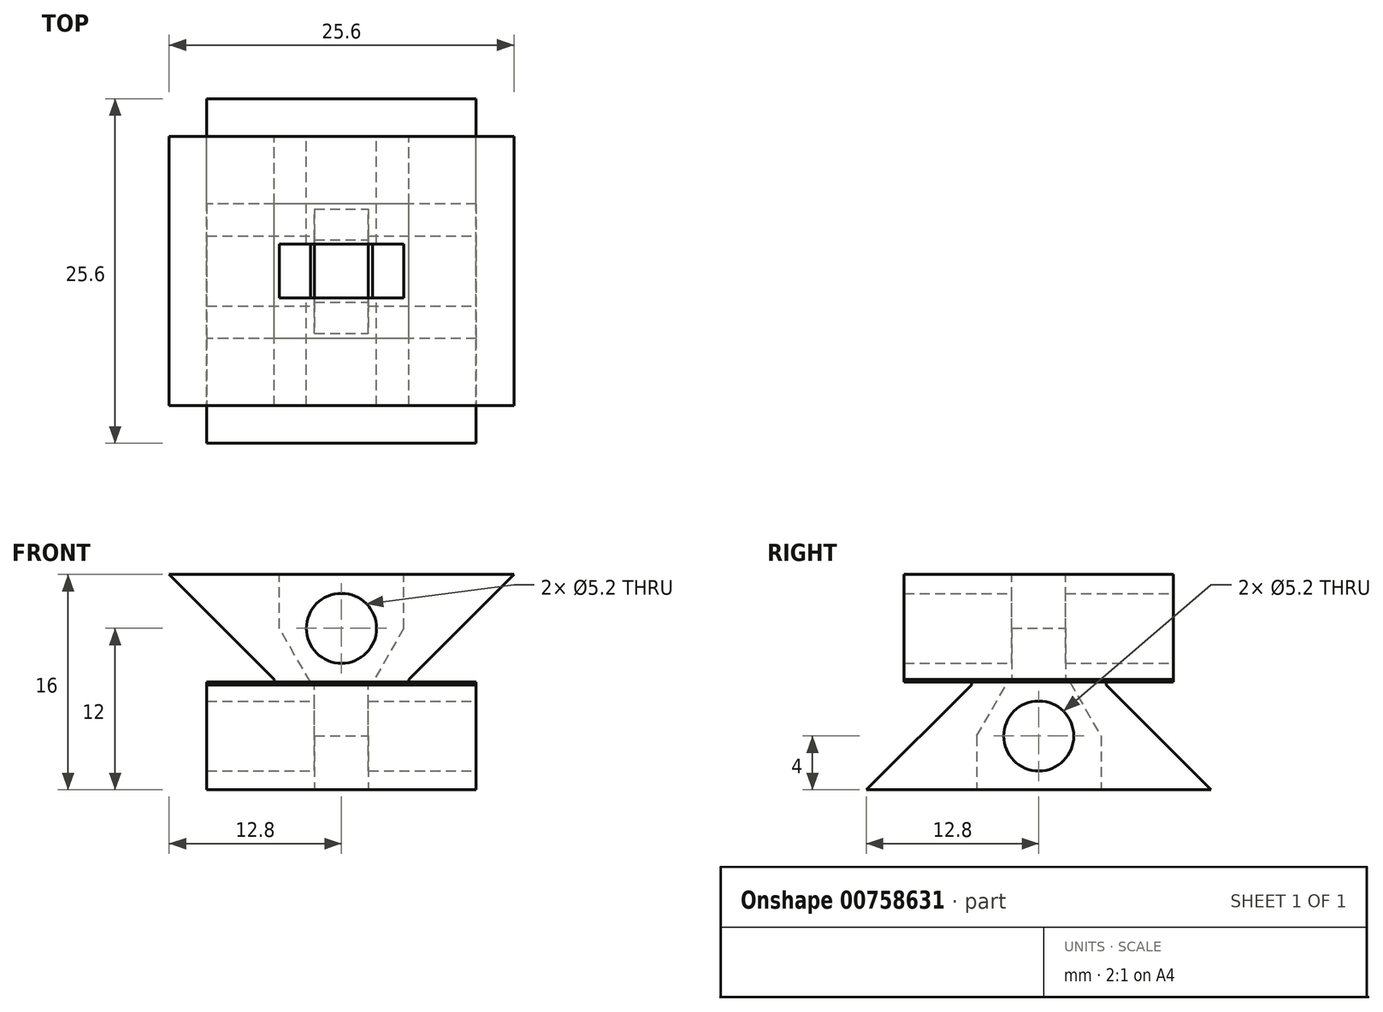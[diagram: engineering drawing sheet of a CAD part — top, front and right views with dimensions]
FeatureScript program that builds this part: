
annotation { "Feature Type Name" : "Feature", "Feature Type Description" : "" }
export const myFeature = defineFeature(function(context is Context, id is Id, definition is map)
    precondition{}
    {
        {
            var Q0;
            Q0=qCreatedBy(makeId("Front.planeOp"),FACE);
            var sketch = newSketch(context, id + "F0", { "sketchPlane" : qUnion([Q0])});
            skLineSegment(sketch, "E0", {"start": v(0, 8) * mm, "end": v(12.8, 8) * mm});
            skLineSegment(sketch, "E1", {"start": v(12.8, 8) * mm, "end": v(5, 0.2) * mm});
            skLineSegment(sketch, "E2.MirrorCS", {"start": v(0, 8) * mm, "end": v(-12.8, 8) * mm});
            skLineSegment(sketch, "E3.MirrorCS", {"start": v(-12.8, 8) * mm, "end": v(-5, 0.2) * mm});
            skLineSegment(sketch, "E4", {"start": v(5, 0.2) * mm, "end": v(5, 0) * mm});
            skLineSegment(sketch, "E5", {"start": v(5, 0) * mm, "end": v(0, 0) * mm});
            skLineSegment(sketch, "E6.MirrorCS", {"start": v(-5, 0.2) * mm, "end": v(-5, 0) * mm});
            skLineSegment(sketch, "E7.MirrorCS", {"start": v(-5, 0) * mm, "end": v(0, 0) * mm});
            skSolve(sketch);
        }
        {
            var Q0;
            Q0=makeQuery(id+"F0.imprint","IMPRINT",FACE,{"disambiguationData":[TD([[makeQuery(id+"F0.imprint","IMPRINT",EDGE,{"derivedFrom":sQuery(id+"F0.wireOp",EDGE,"E0")}),-1.0]])]});
            extrude(context, id + "F1", {"entities" : qUnion([Q0]), "depth" : 20 * mm, "offsetDistance" : 25 * mm, "symmetric" : true});
        }
        {
            var Q0;
            Q0=qCreatedBy(makeId("Right.planeOp"),FACE);
            var sketch = newSketch(context, id + "F2", { "sketchPlane" : qUnion([Q0])});
            skLineSegment(sketch, "E8.MirrorCS", {"start": v(-5, -0.2) * mm, "end": v(-12.8, -8) * mm});
            skLineSegment(sketch, "E9.MirrorCS", {"start": v(-12.8, -8) * mm, "end": v(0, -8) * mm});
            skLineSegment(sketch, "E10", {"start": v(-5, -0.2) * mm, "end": v(-5, 0) * mm});
            skLineSegment(sketch, "E11", {"start": v(-5, 0) * mm, "end": v(0, 0) * mm});
            skLineSegment(sketch, "E12.MirrorCS", {"start": v(5, 0) * mm, "end": v(0, 0) * mm});
            skLineSegment(sketch, "E13.MirrorCS", {"start": v(5, -0.2) * mm, "end": v(5, 0) * mm});
            skLineSegment(sketch, "E14.MirrorCS", {"start": v(5, -0.2) * mm, "end": v(12.8, -8) * mm});
            skLineSegment(sketch, "E15.MirrorCS", {"start": v(12.8, -8) * mm, "end": v(0, -8) * mm});
            skSolve(sketch);
        }
        {
            var Q0;
            Q0=qCreatedBy(makeId("Front.planeOp"),FACE);
            var sketch = newSketch(context, id + "F3", { "sketchPlane" : qUnion([Q0])});
            skLineSegment(sketch, "E16.1", {"start": v(4.62, 4) * mm, "end": v(2.3, 0) * mm});
            skLineSegment(sketch, "E16.2", {"start": v(2.3, 0) * mm, "end": v(-2.3, 0) * mm});
            skLineSegment(sketch, "E16.3", {"start": v(-2.3, 0) * mm, "end": v(-4.62, 4) * mm});
            skLineSegment(sketch, "E17.top", {"start": v(-4.62, 8) * mm, "end": v(4.62, 8) * mm});
            skLineSegment(sketch, "E17.left", {"start": v(-4.62, 4) * mm, "end": v(-4.62, 8) * mm});
            skLineSegment(sketch, "E17.right", {"start": v(4.62, 4) * mm, "end": v(4.62, 8) * mm});
            skSolve(sketch);
        }
        {
            var Q0;
            Q0 = qSketchRegion(id + "F3", true);
            extrude(context, id + "F4", {"entities" : qUnion([Q0]), "operationType" : NewBodyOperationType.REMOVE, "depth" : 4 * mm, "offsetDistance" : 25 * mm, "symmetric" : true});
        }
        {
            var Q0;
            Q0=qCreatedBy(makeId("Right.planeOp"),FACE);
            var sketch = newSketch(context, id + "F5", { "sketchPlane" : qUnion([Q0])});
            skLineSegment(sketch, "E18.1", {"start": v(-4.62, -4) * mm, "end": v(-2.3, 0) * mm});
            skLineSegment(sketch, "E18.2", {"start": v(-2.3, 0) * mm, "end": v(2.3, 0) * mm});
            skLineSegment(sketch, "E18.3", {"start": v(2.3, 0) * mm, "end": v(4.62, -4) * mm});
            skLineSegment(sketch, "E19.top", {"start": v(4.62, -8) * mm, "end": v(-4.62, -8) * mm});
            skLineSegment(sketch, "E19.left", {"start": v(4.62, -4) * mm, "end": v(4.62, -8) * mm});
            skLineSegment(sketch, "E19.right", {"start": v(-4.62, -4) * mm, "end": v(-4.62, -8) * mm});
            skSolve(sketch);
        }
        {
            var Q0;
            Q0=qCreatedBy(makeId("Right.planeOp"),FACE);
            var sketch = newSketch(context, id + "F6", { "sketchPlane" : qUnion([Q0])});
            skCircle(sketch, "E20", {"center": v(0, -4) * mm, "radius": 2.6 * mm});
            skSolve(sketch);
        }
        {
            var Q0;
            Q0=qCreatedBy(makeId("Front.planeOp"),FACE);
            var sketch = newSketch(context, id + "F7", { "sketchPlane" : qUnion([Q0])});
            skCircle(sketch, "E21", {"center": v(0, 4) * mm, "radius": 2.6 * mm});
            skSolve(sketch);
        }
        {
            var Q0;
            Q0 = qSketchRegion(id + "F7", true);
            extrude(context, id + "F8", {"entities" : qUnion([Q0]), "operationType" : NewBodyOperationType.REMOVE, "depth" : 20 * mm, "offsetDistance" : 25 * mm, "symmetric" : true});
        }
        {
            var Q0;
            Q0=makeQuery(id+"F2.imprint","IMPRINT",FACE,{"disambiguationData":[TD([[makeQuery(id+"F2.imprint","IMPRINT",EDGE,{"derivedFrom":sQuery(id+"F2.wireOp",EDGE,"E8.MirrorCS")}),1.0]])]});
            extrude(context, id + "F9", {"entities" : qUnion([Q0]), "operationType" : NewBodyOperationType.ADD, "depth" : 20 * mm, "offsetDistance" : 25 * mm, "symmetric" : true});
        }
        {
            var Q0;
            Q0 = qSketchRegion(id + "F5", true);
            extrude(context, id + "F10", {"entities" : qUnion([Q0]), "operationType" : NewBodyOperationType.REMOVE, "oppositeDirection" : true, "depth" : 4 * mm, "offsetDistance" : 25 * mm, "symmetric" : true});
        }
        {
            var Q0;
            Q0 = qSketchRegion(id + "F6", true);
            extrude(context, id + "F11", {"entities" : qUnion([Q0]), "operationType" : NewBodyOperationType.REMOVE, "oppositeDirection" : true, "depth" : 20 * mm, "offsetDistance" : 25 * mm, "symmetric" : true});
        }
    });
